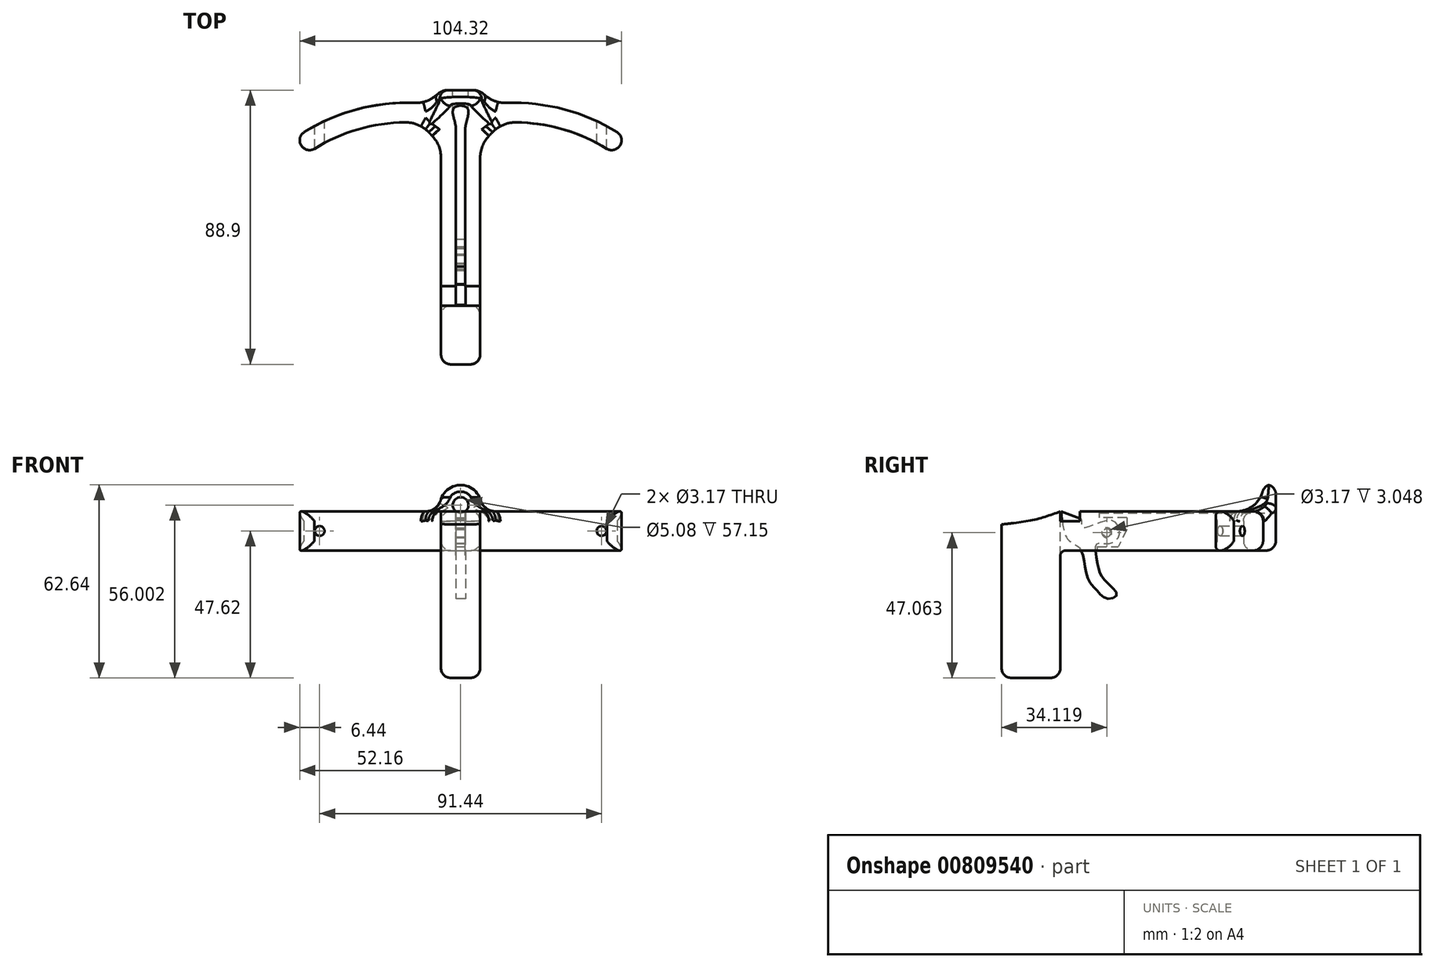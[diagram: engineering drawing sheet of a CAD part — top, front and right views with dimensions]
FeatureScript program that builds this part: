
annotation { "Feature Type Name" : "Feature", "Feature Type Description" : "" }
export const myFeature = defineFeature(function(context is Context, id is Id, definition is map)
    precondition{}
    {
        {
            var Q0;
            Q0=qCreatedBy(makeId("Top.planeOp"),FACE);
            var sketch = newSketch(context, id + "F0", { "sketchPlane" : qUnion([Q0])});
            skLineSegment(sketch, "E0.bottom", {"start": v(0, 0) * mm, "end": v(6.35, 0) * mm});
            skLineSegment(sketch, "E0.top", {"start": v(0, 76.2) * mm, "end": v(6.35, 76.2) * mm});
            skLineSegment(sketch, "E0.left", {"start": v(0, 0) * mm, "end": v(0, 76.2) * mm});
            skLineSegment(sketch, "E0.right", {"start": v(6.35, 0) * mm, "end": v(6.35, 58.42) * mm});
            skArc(sketch, "E1", {"start": v(50.8, 62.54) * mm, "mid": v(29.37, 70.92) * mm, "end": v(6.35, 71.12) * mm});
            skArc(sketch, "E2.0", {"start": v(47.45, 57.14) * mm, "mid": v(31.06, 64.05) * mm, "end": v(13.33, 65.59) * mm});
            skLineSegment(sketch, "E3", {"start": v(6.35, 58.42) * mm, "end": v(13.33, 65.59) * mm});
            skArc(sketch, "E4", {"start": v(47.45, 57.14) * mm, "mid": v(51.68, 58.26) * mm, "end": v(50.8, 62.54) * mm});
            skLineSegment(sketch, "E5.trimOffspring", {"start": v(6.35, 71.12) * mm, "end": v(6.35, 76.2) * mm});
            skLineSegment(sketch, "E6.MirrorCS", {"start": v(-6.35, 71.12) * mm, "end": v(-6.35, 76.2) * mm});
            skArc(sketch, "E7.MirrorCS", {"start": v(-47.45, 57.14) * mm, "mid": v(-51.68, 58.26) * mm, "end": v(-50.8, 62.54) * mm});
            skLineSegment(sketch, "E8.MirrorCS", {"start": v(-6.35, 58.42) * mm, "end": v(-13.34, 65.59) * mm});
            skArc(sketch, "E9.MirrorCS", {"start": v(-47.45, 57.14) * mm, "mid": v(-31.06, 64.05) * mm, "end": v(-13.34, 65.59) * mm});
            skArc(sketch, "E10.MirrorCS", {"start": v(-50.8, 62.54) * mm, "mid": v(-29.37, 70.92) * mm, "end": v(-6.35, 71.12) * mm});
            skLineSegment(sketch, "E11.MirrorCS", {"start": v(-6.35, 0) * mm, "end": v(-6.35, 58.42) * mm});
            skLineSegment(sketch, "E12", {"start": v(-6.35, 76.2) * mm, "end": v(0, 76.2) * mm});
            skLineSegment(sketch, "E13", {"start": v(-6.35, 0) * mm, "end": v(0, 0) * mm});
            skSolve(sketch);
        }
        {
            var Q0;
            Q0 = qSketchRegion(id + "F0", true);
            extrude(context, id + "F1", {"entities" : qUnion([Q0]), "depth" : 12.7 * mm, "offsetDistance" : 25.4 * mm});
        }
        {
            var Q0;
            Q0=makeQuery(id+"F1.opExtrude","SWEPT_EDGE",EDGE,{"disambiguationData":[OSD([sQuery(id+"F0.wireOp",EDGE,"E2.0"),sQuery(id+"F0.wireOp",EDGE,"E3")])]});
            var Q1;
            Q1=makeQuery(id+"F1.opExtrude","SWEPT_EDGE",EDGE,{"disambiguationData":[OSD([sQuery(id+"F0.wireOp",EDGE,"E0.right"),sQuery(id+"F0.wireOp",EDGE,"E3")])]});
            var Q2;
            Q2=makeQuery(id+"F1.opExtrude","SWEPT_EDGE",EDGE,{"disambiguationData":[OSD([sQuery(id+"F0.wireOp",EDGE,"E1"),sQuery(id+"F0.wireOp",EDGE,"E5.trimOffspring")])]});
            var Q3;
            Q3=makeQuery(id+"F1.opExtrude","SWEPT_EDGE",EDGE,{"disambiguationData":[OSD([sQuery(id+"F0.wireOp",EDGE,"E6.MirrorCS"),sQuery(id+"F0.wireOp",EDGE,"E10.MirrorCS")])]});
            var Q4;
            Q4=makeQuery(id+"F1.opExtrude","SWEPT_EDGE",EDGE,{"disambiguationData":[OSD([sQuery(id+"F0.wireOp",EDGE,"E8.MirrorCS"),sQuery(id+"F0.wireOp",EDGE,"E11.MirrorCS")])]});
            var Q5;
            Q5=makeQuery(id+"F1.opExtrude","SWEPT_EDGE",EDGE,{"disambiguationData":[OSD([sQuery(id+"F0.wireOp",EDGE,"E8.MirrorCS"),sQuery(id+"F0.wireOp",EDGE,"E9.MirrorCS")])]});
            fillet(context, id + "F2", {"entities" : qUnion([Q0, Q1, Q2, Q3, Q4, Q5]), "radius" : 10.16 * mm, "tangentPropagation" : true, "allowEdgeOverflow" : false});
        }
        {
            var Q0;
            Q0=makeQuery(id+"F1.opExtrude","SWEPT_FACE",FACE,{"disambiguationData":[OSD([sQuery(id+"F0.wireOp",EDGE,"E0.top"),sQuery(id+"F0.wireOp",EDGE,"E12")])]});
            var sketch = newSketch(context, id + "F3", { "sketchPlane" : qUnion([Q0])});
            skCircle(sketch, "E14", {"center": v(0, 14.73) * mm, "radius": 6.67 * mm});
            skCircle(sketch, "E15", {"center": v(0, 14.73) * mm, "radius": 2.54 * mm});
            skSolve(sketch);
        }
        {
            var Q0;
            Q0 = qSketchRegion(id + "F3", true);
            extrude(context, id + "F4", {"entities" : qUnion([Q0]), "operationType" : NewBodyOperationType.ADD, "oppositeDirection" : true, "depth" : 12.7 * mm, "offsetDistance" : 25.4 * mm});
        }
        {
            var Q0;
            Q0=qCreatedBy(makeId("Right.planeOp"),FACE);
            var sketch = newSketch(context, id + "F5", { "sketchPlane" : qUnion([Q0])});
            skCircle(sketch, "E16", {"center": v(63.5, 21.4) * mm, "radius": 8.7 * mm});
            skSolve(sketch);
        }
        {
            var Q0;
            Q0 = qSketchRegion(id + "F5", true);
            extrude(context, id + "F6", {"entities" : qUnion([Q0]), "operationType" : NewBodyOperationType.REMOVE, "endBound" : BoundingType.SYMMETRIC, "oppositeDirection" : true, "depth" : 25.4 * mm, "offsetDistance" : 25.4 * mm});
        }
        {
            var Q0;
            Q0=makeQuery(id+"F4.boolean.opBoolean","INTERSECT",EDGE,{"disambiguationData":[OD(0.0)],"derivedFrom":[makeQuery(id+"F1.opExtrude","CAP_FACE",FACE,{"disambiguationData":[OSD([sQuery(id+"F0.wireOp",EDGE,"E0.bottom"),sQuery(id+"F0.wireOp",EDGE,"E0.top"),sQuery(id+"F0.wireOp",EDGE,"E0.right"),sQuery(id+"F0.wireOp",EDGE,"E1"),sQuery(id+"F0.wireOp",EDGE,"E2.0"),sQuery(id+"F0.wireOp",EDGE,"E3"),sQuery(id+"F0.wireOp",EDGE,"E4"),sQuery(id+"F0.wireOp",EDGE,"E5.trimOffspring"),sQuery(id+"F0.wireOp",EDGE,"E6.MirrorCS"),sQuery(id+"F0.wireOp",EDGE,"E7.MirrorCS"),sQuery(id+"F0.wireOp",EDGE,"E8.MirrorCS"),sQuery(id+"F0.wireOp",EDGE,"E9.MirrorCS"),sQuery(id+"F0.wireOp",EDGE,"E10.MirrorCS"),sQuery(id+"F0.wireOp",EDGE,"E11.MirrorCS"),sQuery(id+"F0.wireOp",EDGE,"E12"),sQuery(id+"F0.wireOp",EDGE,"E13")])],"isStart":false}),makeQuery(id+"F4.opExtrude","SWEPT_FACE",FACE,{"disambiguationData":[OSD([sQuery(id+"F3.wireOp",EDGE,"E14")])]})]});
            var Q1;
            Q1=makeQuery(id+"F4.boolean.opBoolean","INTERSECT",EDGE,{"disambiguationData":[OD(1.0)],"derivedFrom":[makeQuery(id+"F1.opExtrude","CAP_FACE",FACE,{"disambiguationData":[OSD([sQuery(id+"F0.wireOp",EDGE,"E0.bottom"),sQuery(id+"F0.wireOp",EDGE,"E0.top"),sQuery(id+"F0.wireOp",EDGE,"E0.right"),sQuery(id+"F0.wireOp",EDGE,"E1"),sQuery(id+"F0.wireOp",EDGE,"E2.0"),sQuery(id+"F0.wireOp",EDGE,"E3"),sQuery(id+"F0.wireOp",EDGE,"E4"),sQuery(id+"F0.wireOp",EDGE,"E5.trimOffspring"),sQuery(id+"F0.wireOp",EDGE,"E6.MirrorCS"),sQuery(id+"F0.wireOp",EDGE,"E7.MirrorCS"),sQuery(id+"F0.wireOp",EDGE,"E8.MirrorCS"),sQuery(id+"F0.wireOp",EDGE,"E9.MirrorCS"),sQuery(id+"F0.wireOp",EDGE,"E10.MirrorCS"),sQuery(id+"F0.wireOp",EDGE,"E11.MirrorCS"),sQuery(id+"F0.wireOp",EDGE,"E12"),sQuery(id+"F0.wireOp",EDGE,"E13")])],"isStart":false}),makeQuery(id+"F4.opExtrude","SWEPT_FACE",FACE,{"disambiguationData":[OSD([sQuery(id+"F3.wireOp",EDGE,"E14")])]})]});
            fillet(context, id + "F7", {"entities" : qUnion([Q0, Q1]), "radius" : 5.08 * mm, "tangentPropagation" : true, "allowEdgeOverflow" : false});
        }
        {
            var Q0;
            Q0=makeQuery(id+"F4.boolean.opBoolean","MERGE",FACE,{"derivedFrom":[makeQuery(id+"F1.opExtrude","SWEPT_FACE",FACE,{"disambiguationData":[OSD([sQuery(id+"F0.wireOp",EDGE,"E0.top"),sQuery(id+"F0.wireOp",EDGE,"E12")])]}),makeQuery(id+"F4.opExtrude","CAP_FACE",FACE,{"disambiguationData":[OSD([sQuery(id+"F3.wireOp",EDGE,"E14"),sQuery(id+"F3.wireOp",EDGE,"E15")])],"isStart":true})]});
            var sketch = newSketch(context, id + "F8", { "sketchPlane" : qUnion([Q0])});
            skCircle(sketch, "E17", {"center": v(0, 14.73) * mm, "radius": 2.54 * mm});
            skSolve(sketch);
        }
        {
            var Q0;
            Q0 = qSketchRegion(id + "F8", true);
            extrude(context, id + "F9", {"entities" : qUnion([Q0]), "operationType" : NewBodyOperationType.REMOVE, "endBound" : BoundingType.THROUGH_ALL, "oppositeDirection" : true, "depth" : 25.4 * mm, "offsetDistance" : 25.4 * mm});
        }
        {
            var Q0;
            Q0=makeQuery(id+"F4.boolean.opBoolean","MERGE",FACE,{"derivedFrom":[makeQuery(id+"F1.opExtrude","SWEPT_FACE",FACE,{"disambiguationData":[OSD([sQuery(id+"F0.wireOp",EDGE,"E0.top"),sQuery(id+"F0.wireOp",EDGE,"E12")])]}),makeQuery(id+"F4.opExtrude","CAP_FACE",FACE,{"disambiguationData":[OSD([sQuery(id+"F3.wireOp",EDGE,"E14"),sQuery(id+"F3.wireOp",EDGE,"E15")])],"isStart":true})]});
            cPlane(context, id + "F10", {"entities" : qUnion([Q0]), "cplaneType" : CPlaneType.OFFSET, "offset" : 0 * mm, "width" : 152.4 * mm, "height" : 152.4 * mm});
        }
        {
            var Q0;
            Q0=makeQuery(id+"F1.opExtrude","SWEPT_FACE",FACE,{"disambiguationData":[OSD([sQuery(id+"F0.wireOp",EDGE,"E11.MirrorCS")])]});
            var sketch = newSketch(context, id + "F11", { "sketchPlane" : qUnion([Q0])});
            skLineSegment(sketch, "E18.bottom", {"start": v(0, 12.7) * mm, "end": v(-12.7, 12.7) * mm});
            skLineSegment(sketch, "E18.top", {"start": v(0, 9.52) * mm, "end": v(-12.7, 9.52) * mm});
            skLineSegment(sketch, "E18.left", {"start": v(0, 12.7) * mm, "end": v(0, 9.52) * mm});
            skLineSegment(sketch, "E18.right", {"start": v(-12.7, 12.7) * mm, "end": v(-12.7, 9.52) * mm});
            skSolve(sketch);
        }
        {
            var Q0;
            Q0 = qSketchRegion(id + "F11", true);
            extrude(context, id + "F12", {"entities" : qUnion([Q0]), "operationType" : NewBodyOperationType.REMOVE, "oppositeDirection" : true, "depth" : 25.4 * mm, "offsetDistance" : 25.4 * mm});
        }
        {
            var Q0;
            {var subQ0=sQuery(id+"F0.wireOp",EDGE,"E9.MirrorCS");var subQ1=sQuery(id+"F0.wireOp",EDGE,"E8.MirrorCS");var subQ2=sQuery(id+"F0.wireOp",EDGE,"E10.MirrorCS");var subQ3=sQuery(id+"F0.wireOp",EDGE,"E11.MirrorCS");var subQ4=sQuery(id+"F0.wireOp",EDGE,"E6.MirrorCS");var subQ5=sQuery(id+"F0.wireOp",EDGE,"E7.MirrorCS");var subQ6=sQuery(id+"F0.wireOp",EDGE,"E13");var subQ7=sQuery(id+"F0.wireOp",EDGE,"E0.bottom");var subQ9=sQuery(id+"F0.wireOp",EDGE,"E12");var subQ10=sQuery(id+"F0.wireOp",EDGE,"E5.trimOffspring");var subQ11=sQuery(id+"F0.wireOp",EDGE,"E4");var subQ12=sQuery(id+"F0.wireOp",EDGE,"E3");var subQ13=sQuery(id+"F0.wireOp",EDGE,"E2.0");var subQ14=sQuery(id+"F0.wireOp",EDGE,"E1");var subQ15=sQuery(id+"F0.wireOp",EDGE,"E0.right");var subQ16=sQuery(id+"F0.wireOp",EDGE,"E0.top");var subQ17=makeQuery(id+"F1.opExtrude","CAP_FACE",FACE,{"disambiguationData":[OSD([subQ7,subQ16,subQ15,subQ14,subQ13,subQ12,subQ11,subQ10,subQ4,subQ5,subQ1,subQ0,subQ2,subQ3,subQ9,subQ6])],"isStart":false});Q0=makeQuery(id+"F9.boolean.opBoolean","SPLIT",FACE,{"disambiguationData":[TD([makeQuery(id+"F1.opExtrude","SWEPT_FACE",FACE,{"disambiguationData":[OSD([subQ5])]})])],"derivedFrom":subQ17});}
            var sketch = newSketch(context, id + "F13", { "sketchPlane" : qUnion([Q0])});
            skLineSegment(sketch, "E19.bottom", {"start": v(-1.52, 19.05) * mm, "end": v(1.52, 19.05) * mm});
            skLineSegment(sketch, "E19.top", {"start": v(-1.52, 6.35) * mm, "end": v(1.52, 6.35) * mm});
            skLineSegment(sketch, "E19.left", {"start": v(-1.52, 19.05) * mm, "end": v(-1.52, 6.35) * mm});
            skLineSegment(sketch, "E19.right", {"start": v(1.52, 19.05) * mm, "end": v(1.52, 6.35) * mm});
            skSolve(sketch);
        }
        {
            var Q0;
            Q0 = qSketchRegion(id + "F13", true);
            extrude(context, id + "F14", {"entities" : qUnion([Q0]), "operationType" : NewBodyOperationType.REMOVE, "oppositeDirection" : true, "depth" : 25.4 * mm, "offsetDistance" : 25.4 * mm});
        }
        {
            var Q0;
            Q0=makeQuery(id+"F14.boolean.opBoolean","COPY",FACE,{"derivedFrom":makeQuery(id+"F14.opExtrude","SWEPT_FACE",FACE,{"disambiguationData":[OSD([sQuery(id+"F13.wireOp",EDGE,"E19.right")])]})});
            var Q1;
            Q1=makeQuery(id+"F14.boolean.opBoolean","COPY",FACE,{"derivedFrom":makeQuery(id+"F14.opExtrude","SWEPT_FACE",FACE,{"disambiguationData":[OSD([sQuery(id+"F13.wireOp",EDGE,"E19.left")])]})});
            cPlane(context, id + "F15", {"entities" : qUnion([Q0, Q1]), "cplaneType" : CPlaneType.MID_PLANE, "offset" : 25.4 * mm, "width" : 152.4 * mm, "height" : 152.4 * mm});
        }
        {
            var Q0;
            Q0=makeQuery(id+"F1.opExtrude","SWEPT_FACE",FACE,{"disambiguationData":[OSD([sQuery(id+"F0.wireOp",EDGE,"E0.bottom"),sQuery(id+"F0.wireOp",EDGE,"E13")])]});
            var sketch = newSketch(context, id + "F16", { "sketchPlane" : qUnion([Q0])});
            skPoint(sketch, "E20.oppositeSnap0", {"position": v(6.35, 4.76) * mm});
            skLineSegment(sketch, "E20.bottom", {"start": v(-6.35, 9.52) * mm, "end": v(6.35, 9.52) * mm});
            skLineSegment(sketch, "E20.top", {"start": v(-6.35, -41.28) * mm, "end": v(6.35, -41.28) * mm});
            skLineSegment(sketch, "E20.left", {"start": v(-6.35, 9.52) * mm, "end": v(-6.35, -41.28) * mm});
            skLineSegment(sketch, "E20.right", {"start": v(6.35, 9.52) * mm, "end": v(6.35, -41.28) * mm});
            skSolve(sketch);
        }
        {
            var Q0;
            Q0 = qSketchRegion(id + "F16", true);
            extrude(context, id + "F17", {"entities" : qUnion([Q0]), "operationType" : NewBodyOperationType.ADD, "endBound" : BoundingType.SYMMETRIC, "depth" : 12.7 * mm, "offsetDistance" : 25.4 * mm});
        }
        {
            var Q0;
            Q0=makeQuery(id+"F17.opExtrude","CAP_FACE",FACE,{"disambiguationData":[OSD([sQuery(id+"F16.wireOp",EDGE,"E20.bottom"),sQuery(id+"F16.wireOp",EDGE,"E20.top"),sQuery(id+"F16.wireOp",EDGE,"E20.left"),sQuery(id+"F16.wireOp",EDGE,"E20.right")])],"isStart":false});
            var sketch = newSketch(context, id + "F18", { "sketchPlane" : qUnion([Q0])});
            skLineSegment(sketch, "E21.bottom", {"start": v(-6.35, 9.52) * mm, "end": v(6.35, 9.52) * mm});
            skLineSegment(sketch, "E21.top", {"start": v(-6.35, -41.28) * mm, "end": v(6.35, -41.28) * mm});
            skLineSegment(sketch, "E21.left", {"start": v(-6.35, 9.52) * mm, "end": v(-6.35, -41.28) * mm});
            skLineSegment(sketch, "E21.right", {"start": v(6.35, 9.52) * mm, "end": v(6.35, -41.28) * mm});
            skSolve(sketch);
        }
        {
            var Q0;
            Q0 = qSketchRegion(id + "F18", true);
            extrude(context, id + "F19", {"entities" : qUnion([Q0]), "operationType" : NewBodyOperationType.ADD, "depth" : 6.35 * mm, "offsetDistance" : 25.4 * mm});
        }
        {
            var Q0;
            Q0=makeQuery(id+"F19.boolean.opBoolean","MERGE",FACE,{"derivedFrom":[makeQuery(id+"F17.boolean.opBoolean","MERGE",FACE,{"derivedFrom":[makeQuery(id+"F12.boolean.opBoolean","COPY",FACE,{"derivedFrom":makeQuery(id+"F12.opExtrude","SWEPT_FACE",FACE,{"disambiguationData":[OSD([sQuery(id+"F11.wireOp",EDGE,"E18.top")])]})}),makeQuery(id+"F17.opExtrude","SWEPT_FACE",FACE,{"disambiguationData":[OSD([sQuery(id+"F16.wireOp",EDGE,"E20.bottom")])]})]}),makeQuery(id+"F19.opExtrude","SWEPT_FACE",FACE,{"disambiguationData":[OSD([sQuery(id+"F18.wireOp",EDGE,"E21.bottom")])]})]});
            var sketch = newSketch(context, id + "F20", { "sketchPlane" : qUnion([Q0])});
            skLineSegment(sketch, "E22.bottom", {"start": v(-6.35, 6.35) * mm, "end": v(6.35, 6.35) * mm});
            skLineSegment(sketch, "E22.top", {"start": v(-6.35, -12.7) * mm, "end": v(6.35, -12.7) * mm});
            skLineSegment(sketch, "E22.left", {"start": v(-6.35, 6.35) * mm, "end": v(-6.35, -12.7) * mm});
            skLineSegment(sketch, "E22.right", {"start": v(6.35, 6.35) * mm, "end": v(6.35, -12.7) * mm});
            skSolve(sketch);
        }
        {
            var Q0;
            Q0 = qSketchRegion(id + "F20", true);
            extrude(context, id + "F21", {"entities" : qUnion([Q0]), "operationType" : NewBodyOperationType.ADD, "depth" : 3.17 * mm, "offsetDistance" : 25.4 * mm});
        }
        {
            var Q0;
            Q0=makeQuery(id+"F21.boolean.opBoolean","MERGE",FACE,{"derivedFrom":[makeQuery(id+"F19.boolean.opBoolean","MERGE",FACE,{"derivedFrom":[makeQuery(id+"F17.boolean.opBoolean","MERGE",FACE,{"derivedFrom":[makeQuery(id+"F1.opExtrude","SWEPT_FACE",FACE,{"disambiguationData":[OSD([sQuery(id+"F0.wireOp",EDGE,"E11.MirrorCS")])]}),makeQuery(id+"F17.opExtrude","SWEPT_FACE",FACE,{"disambiguationData":[OSD([sQuery(id+"F16.wireOp",EDGE,"E20.left")])]})]}),makeQuery(id+"F19.opExtrude","SWEPT_FACE",FACE,{"disambiguationData":[OSD([sQuery(id+"F18.wireOp",EDGE,"E21.left")])]})]}),makeQuery(id+"F21.opExtrude","SWEPT_FACE",FACE,{"disambiguationData":[OSD([sQuery(id+"F20.wireOp",EDGE,"E22.left")])]})]});
            var sketch = newSketch(context, id + "F22", { "sketchPlane" : qUnion([Q0])});
            skFitSpline(sketch, "E23", {"points": [v(-6.35, 12.7) * mm, v(1.52, 10.14) * mm, v(12.7, 8.48) * mm], "startDerivative": vector(16.21, -6.14) * mm, "endDerivative": vector(21.74, -2.4) * mm});
            skLineSegment(sketch, "E24", {"start": v(-6.35, 12.7) * mm, "end": v(12.7, 12.7) * mm});
            skLineSegment(sketch, "E25", {"start": v(12.7, 12.7) * mm, "end": v(12.7, 8.48) * mm});
            skSolve(sketch);
        }
        {
            var Q0;
            Q0 = qSketchRegion(id + "F22", true);
            extrude(context, id + "F23", {"entities" : qUnion([Q0]), "operationType" : NewBodyOperationType.REMOVE, "oppositeDirection" : true, "depth" : 25.4 * mm, "offsetDistance" : 25.4 * mm});
        }
        {
            var Q0;
            Q0=makeQuery(id+"F14.boolean.opBoolean","COPY",FACE,{"derivedFrom":makeQuery(id+"F14.opExtrude","SWEPT_FACE",FACE,{"disambiguationData":[OSD([sQuery(id+"F13.wireOp",EDGE,"E19.bottom")])]})});
            var sketch = newSketch(context, id + "F24", { "sketchPlane" : qUnion([Q0])});
            skLineSegment(sketch, "E26.bottom", {"start": v(-1.52, 10.67) * mm, "end": v(1.52, 10.67) * mm});
            skLineSegment(sketch, "E26.top", {"start": v(-1.52, -2.03) * mm, "end": v(1.52, -2.03) * mm});
            skLineSegment(sketch, "E26.left", {"start": v(-1.52, 10.67) * mm, "end": v(-1.52, -2.03) * mm});
            skLineSegment(sketch, "E26.right", {"start": v(1.52, 10.67) * mm, "end": v(1.52, -2.03) * mm});
            skSolve(sketch);
        }
        {
            var Q0;
            Q0 = qSketchRegion(id + "F24", true);
            extrude(context, id + "F25", {"entities" : qUnion([Q0]), "operationType" : NewBodyOperationType.REMOVE, "oppositeDirection" : true, "depth" : 8.9 * mm, "offsetDistance" : 25.4 * mm});
        }
        {
            var Q0;
            Q0=qCreatedBy(id+"F15.planeOp",FACE);
            var sketch = newSketch(context, id + "F26", { "sketchPlane" : qUnion([Q0])});
            skLineSegment(sketch, "E27", {"start": v(-13.17, 10.28) * mm, "end": v(-6.6, 12.66) * mm});
            skFitSpline(sketch, "E28", {"points": [v(-6.6, 12.66) * mm, v(-7.5, 6.64) * mm, v(-9.13, 3.26) * mm, v(-12.38, 1.03) * mm, v(-14.18, -3.58) * mm, v(-15.37, -9.36) * mm, v(-18.5, -13.27) * mm, v(-21.38, -15.56) * mm, v(-24.62, -14.47) * mm, v(-22.21, -11.02) * mm, v(-19.36, -7.7) * mm, v(-18.42, -4) * mm, v(-18.1, 2.1) * mm, v(-21.6, 2.22) * mm, v(-25.35, 4.8) * mm, v(-22.97, 9.73) * mm, v(-13.49, 7.53) * mm, v(-13.17, 10.28) * mm], "startDerivative": vector(-8.92, -104.87) * mm, "endDerivative": vector(31, 20.67) * mm});
            skCircle(sketch, "E29", {"center": v(-21.42, 5.8) * mm, "radius": 1.59 * mm});
            skSolve(sketch);
        }
        {
            var Q0;
            Q0 = qSketchRegion(id + "F26", true);
            extrude(context, id + "F27", {"entities" : qUnion([Q0]), "operationType" : NewBodyOperationType.ADD, "endBound" : BoundingType.SYMMETRIC, "depth" : 3.17 * mm, "offsetDistance" : 25.4 * mm});
        }
        {
            var Q0;
            Q0=qCreatedBy(id+"F15.planeOp",FACE);
            var sketch = newSketch(context, id + "F28", { "sketchPlane" : qUnion([Q0])});
            skCircle(sketch, "E30", {"center": v(-21.44, 5.77) * mm, "radius": 1.27 * mm});
            skSolve(sketch);
        }
        {
            var Q0;
            Q0 = qSketchRegion(id + "F28", true);
            extrude(context, id + "F29", {"entities" : qUnion([Q0]), "operationType" : NewBodyOperationType.ADD, "endBound" : BoundingType.SYMMETRIC, "depth" : 6.35 * mm, "offsetDistance" : 25.4 * mm});
        }
        {
            var Q0;
            Q0=makeQuery(id+"F25.boolean.opBoolean","MERGE",FACE,{"derivedFrom":[makeQuery(id+"F14.boolean.opBoolean","COPY",FACE,{"derivedFrom":makeQuery(id+"F14.opExtrude","SWEPT_FACE",FACE,{"disambiguationData":[OSD([sQuery(id+"F13.wireOp",EDGE,"E19.right")])]})}),makeQuery(id+"F25.opExtrude","SWEPT_FACE",FACE,{"disambiguationData":[OSD([sQuery(id+"F24.wireOp",EDGE,"E26.right")])]})]});
            var sketch = newSketch(context, id + "F30", { "sketchPlane" : qUnion([Q0])});
            skLineSegment(sketch, "E31.bottom", {"start": v(-27.94, 0) * mm, "end": v(-18.29, 0) * mm});
            skLineSegment(sketch, "E31.top", {"start": v(-27.94, 1.27) * mm, "end": v(-18.29, 1.27) * mm});
            skLineSegment(sketch, "E31.left", {"start": v(-27.94, 0) * mm, "end": v(-27.94, 1.27) * mm});
            skLineSegment(sketch, "E31.right", {"start": v(-18.29, 0) * mm, "end": v(-18.29, 1.27) * mm});
            skLineSegment(sketch, "E32", {"start": v(-25.11, 1.27) * mm, "end": v(-27.94, 6.83) * mm});
            skLineSegment(sketch, "E33", {"start": v(-27.94, 6.83) * mm, "end": v(-27.94, 1.27) * mm});
            skSolve(sketch);
        }
        {
            var Q0;
            Q0 = qSketchRegion(id + "F30", true);
            extrude(context, id + "F31", {"entities" : qUnion([Q0]), "operationType" : NewBodyOperationType.ADD, "depth" : 6.35 * mm, "offsetDistance" : 25.4 * mm});
        }
        {
            var Q0;
            {var subQ0=sQuery(id+"F0.wireOp",EDGE,"E11.MirrorCS");var subQ1=sQuery(id+"F11.wireOp",EDGE,"E18.right");Q0=makeQuery(id+"F12.boolean.opBoolean","COPY",EDGE,{"disambiguationData":[TD([makeQuery(id+"F1.opExtrude","SWEPT_FACE",FACE,{"disambiguationData":[OSD([subQ0])]})])],"derivedFrom":makeQuery(id+"F12.opExtrude","SWEPT_EDGE",EDGE,{"disambiguationData":[OSD([subQ0,sQuery(id+"F11.wireOp",EDGE,"E18.bottom"),subQ1])]})});}
            var Q1;
            {var subQ0=sQuery(id+"F0.wireOp",EDGE,"E11.MirrorCS");var subQ1=sQuery(id+"F0.wireOp",EDGE,"E0.right");var subQ2=sQuery(id+"F11.wireOp",EDGE,"E18.right");Q1=makeQuery(id+"F12.boolean.opBoolean","COPY",EDGE,{"disambiguationData":[TD([makeQuery(id+"F1.opExtrude","SWEPT_FACE",FACE,{"disambiguationData":[OSD([subQ1])]})])],"derivedFrom":makeQuery(id+"F12.opExtrude","SWEPT_EDGE",EDGE,{"disambiguationData":[OSD([subQ0,sQuery(id+"F11.wireOp",EDGE,"E18.bottom"),subQ2])]})});}
            var Q2;
            Q2=makeQuery(id+"F23.boolean.opBoolean","COPY",EDGE,{"derivedFrom":makeQuery(id+"F23.opExtrude","SWEPT_EDGE",EDGE,{"disambiguationData":[OSD([sQuery(id+"F18.wireOp",EDGE,"E21.left"),sQuery(id+"F20.wireOp",EDGE,"E22.top"),sQuery(id+"F20.wireOp",EDGE,"E22.left"),sQuery(id+"F22.wireOp",EDGE,"E23"),sQuery(id+"F22.wireOp",EDGE,"E25")])]})});
            var Q3;
            Q3=makeQuery(id+"F17.boolean.opBoolean","INTERSECT",EDGE,{"disambiguationData":[OD(0.0)],"derivedFrom":[makeQuery(id+"F1.opExtrude","CAP_FACE",FACE,{"disambiguationData":[OSD([sQuery(id+"F0.wireOp",EDGE,"E0.bottom"),sQuery(id+"F0.wireOp",EDGE,"E0.top"),sQuery(id+"F0.wireOp",EDGE,"E0.right"),sQuery(id+"F0.wireOp",EDGE,"E1"),sQuery(id+"F0.wireOp",EDGE,"E2.0"),sQuery(id+"F0.wireOp",EDGE,"E3"),sQuery(id+"F0.wireOp",EDGE,"E4"),sQuery(id+"F0.wireOp",EDGE,"E5.trimOffspring"),sQuery(id+"F0.wireOp",EDGE,"E6.MirrorCS"),sQuery(id+"F0.wireOp",EDGE,"E7.MirrorCS"),sQuery(id+"F0.wireOp",EDGE,"E8.MirrorCS"),sQuery(id+"F0.wireOp",EDGE,"E9.MirrorCS"),sQuery(id+"F0.wireOp",EDGE,"E10.MirrorCS"),sQuery(id+"F0.wireOp",EDGE,"E11.MirrorCS"),sQuery(id+"F0.wireOp",EDGE,"E12"),sQuery(id+"F0.wireOp",EDGE,"E13")])],"isStart":true}),makeQuery(id+"F17.opExtrude","CAP_FACE",FACE,{"disambiguationData":[OSD([sQuery(id+"F16.wireOp",EDGE,"E20.bottom"),sQuery(id+"F16.wireOp",EDGE,"E20.top"),sQuery(id+"F16.wireOp",EDGE,"E20.left"),sQuery(id+"F16.wireOp",EDGE,"E20.right")])],"isStart":true})]});
            var Q4;
            Q4=makeQuery(id+"F17.boolean.opBoolean","INTERSECT",EDGE,{"disambiguationData":[OD(1.0)],"derivedFrom":[makeQuery(id+"F1.opExtrude","CAP_FACE",FACE,{"disambiguationData":[OSD([sQuery(id+"F0.wireOp",EDGE,"E0.bottom"),sQuery(id+"F0.wireOp",EDGE,"E0.top"),sQuery(id+"F0.wireOp",EDGE,"E0.right"),sQuery(id+"F0.wireOp",EDGE,"E1"),sQuery(id+"F0.wireOp",EDGE,"E2.0"),sQuery(id+"F0.wireOp",EDGE,"E3"),sQuery(id+"F0.wireOp",EDGE,"E4"),sQuery(id+"F0.wireOp",EDGE,"E5.trimOffspring"),sQuery(id+"F0.wireOp",EDGE,"E6.MirrorCS"),sQuery(id+"F0.wireOp",EDGE,"E7.MirrorCS"),sQuery(id+"F0.wireOp",EDGE,"E8.MirrorCS"),sQuery(id+"F0.wireOp",EDGE,"E9.MirrorCS"),sQuery(id+"F0.wireOp",EDGE,"E10.MirrorCS"),sQuery(id+"F0.wireOp",EDGE,"E11.MirrorCS"),sQuery(id+"F0.wireOp",EDGE,"E12"),sQuery(id+"F0.wireOp",EDGE,"E13")])],"isStart":true}),makeQuery(id+"F17.opExtrude","CAP_FACE",FACE,{"disambiguationData":[OSD([sQuery(id+"F16.wireOp",EDGE,"E20.bottom"),sQuery(id+"F16.wireOp",EDGE,"E20.top"),sQuery(id+"F16.wireOp",EDGE,"E20.left"),sQuery(id+"F16.wireOp",EDGE,"E20.right")])],"isStart":true})]});
            fillet(context, id + "F32", {"entities" : qUnion([Q0, Q1, Q2, Q3, Q4]), "radius" : 1.59 * mm, "tangentPropagation" : true, "allowEdgeOverflow" : false});
        }
        {
            var Q0;
            Q0=makeQuery(id+"F21.boolean.opBoolean","MERGE",EDGE,{"derivedFrom":[makeQuery(id+"F19.opExtrude","CAP_EDGE",EDGE,{"disambiguationData":[OSD([sQuery(id+"F18.wireOp",EDGE,"E21.left")])],"isStart":false}),makeQuery(id+"F21.opExtrude","SWEPT_EDGE",EDGE,{"disambiguationData":[OSD([sQuery(id+"F20.wireOp",EDGE,"E22.top"),sQuery(id+"F20.wireOp",EDGE,"E22.left")])]})]});
            var Q1;
            Q1=makeQuery(id+"F21.boolean.opBoolean","MERGE",EDGE,{"derivedFrom":[makeQuery(id+"F19.opExtrude","CAP_EDGE",EDGE,{"disambiguationData":[OSD([sQuery(id+"F18.wireOp",EDGE,"E21.right")])],"isStart":false}),makeQuery(id+"F21.opExtrude","SWEPT_EDGE",EDGE,{"disambiguationData":[OSD([sQuery(id+"F20.wireOp",EDGE,"E22.top"),sQuery(id+"F20.wireOp",EDGE,"E22.right")])]})]});
            var Q2;
            Q2=makeQuery(id+"F17.opExtrude","CAP_EDGE",EDGE,{"disambiguationData":[OSD([sQuery(id+"F16.wireOp",EDGE,"E20.left")])],"isStart":true});
            var Q3;
            Q3=makeQuery(id+"F17.opExtrude","CAP_EDGE",EDGE,{"disambiguationData":[OSD([sQuery(id+"F16.wireOp",EDGE,"E20.right")])],"isStart":true});
            var Q4;
            Q4=makeQuery(id+"F19.boolean.opBoolean","MERGE",EDGE,{"derivedFrom":[makeQuery(id+"F17.opExtrude","SWEPT_EDGE",EDGE,{"disambiguationData":[OSD([sQuery(id+"F16.wireOp",EDGE,"E20.top"),sQuery(id+"F16.wireOp",EDGE,"E20.right")])]}),makeQuery(id+"F19.opExtrude","SWEPT_EDGE",EDGE,{"disambiguationData":[OSD([sQuery(id+"F18.wireOp",EDGE,"E21.top"),sQuery(id+"F18.wireOp",EDGE,"E21.right")])]})]});
            var Q5;
            Q5=makeQuery(id+"F17.opExtrude","CAP_EDGE",EDGE,{"disambiguationData":[OSD([sQuery(id+"F16.wireOp",EDGE,"E20.top")])],"isStart":true});
            var Q6;
            Q6=makeQuery(id+"F19.opExtrude","CAP_EDGE",EDGE,{"disambiguationData":[OSD([sQuery(id+"F18.wireOp",EDGE,"E21.top")])],"isStart":false});
            var Q7;
            Q7=makeQuery(id+"F19.boolean.opBoolean","MERGE",EDGE,{"derivedFrom":[makeQuery(id+"F17.opExtrude","SWEPT_EDGE",EDGE,{"disambiguationData":[OSD([sQuery(id+"F16.wireOp",EDGE,"E20.top"),sQuery(id+"F16.wireOp",EDGE,"E20.left")])]}),makeQuery(id+"F19.opExtrude","SWEPT_EDGE",EDGE,{"disambiguationData":[OSD([sQuery(id+"F18.wireOp",EDGE,"E21.top"),sQuery(id+"F18.wireOp",EDGE,"E21.left")])]})]});
            var Q8;
            Q8=makeQuery(id+"F1.opExtrude","CAP_EDGE",EDGE,{"disambiguationData":[OSD([sQuery(id+"F0.wireOp",EDGE,"E1")])],"isStart":true});
            var Q9;
            Q9=makeQuery(id+"F1.opExtrude","CAP_EDGE",EDGE,{"disambiguationData":[OSD([sQuery(id+"F0.wireOp",EDGE,"E0.top"),sQuery(id+"F0.wireOp",EDGE,"E12")])],"isStart":true});
            var Q10;
            Q10=makeQuery(id+"F1.opExtrude","CAP_EDGE",EDGE,{"disambiguationData":[OSD([sQuery(id+"F0.wireOp",EDGE,"E10.MirrorCS")])],"isStart":true});
            var Q11;
            Q11=makeQuery(id+"F1.opExtrude","CAP_EDGE",EDGE,{"disambiguationData":[OSD([sQuery(id+"F0.wireOp",EDGE,"E9.MirrorCS")])],"isStart":false});
            var Q12;
            Q12=makeQuery(id+"F1.opExtrude","CAP_EDGE",EDGE,{"disambiguationData":[OSD([sQuery(id+"F0.wireOp",EDGE,"E10.MirrorCS")])],"isStart":false});
            var Q13;
            Q13=makeQuery(id+"F1.opExtrude","CAP_EDGE",EDGE,{"disambiguationData":[OSD([sQuery(id+"F0.wireOp",EDGE,"E2.0")])],"isStart":false});
            var Q14;
            Q14=makeQuery(id+"F1.opExtrude","CAP_EDGE",EDGE,{"disambiguationData":[OSD([sQuery(id+"F0.wireOp",EDGE,"E1")])],"isStart":false});
            var Q15;
            Q15=makeQuery(id+"F4.opExtrude","CAP_EDGE",EDGE,{"disambiguationData":[OSD([sQuery(id+"F3.wireOp",EDGE,"E14")])],"isStart":true});
            var Q16;
            Q16=makeQuery(id+"F6.boolean.opBoolean","INTERSECT",EDGE,{"derivedFrom":[makeQuery(id+"F4.opExtrude","SWEPT_FACE",FACE,{"disambiguationData":[OSD([sQuery(id+"F3.wireOp",EDGE,"E14")])]}),makeQuery(id+"F6.opExtrude","SWEPT_FACE",FACE,{"disambiguationData":[OSD([sQuery(id+"F5.wireOp",EDGE,"E16")])]})]});
            fillet(context, id + "F33", {"entities" : qUnion([Q0, Q1, Q2, Q3, Q4, Q5, Q6, Q7, Q8, Q9, Q10, Q11, Q12, Q13, Q14, Q15, Q16]), "radius" : 3.17 * mm, "tangentPropagation" : true, "allowEdgeOverflow" : false});
        }
        {
            var Q0;
            Q0=qCreatedBy(id+"F10.planeOp",FACE);
            var sketch = newSketch(context, id + "F34", { "sketchPlane" : qUnion([Q0])});
            skCircle(sketch, "E34", {"center": v(-45.72, 6.35) * mm, "radius": 1.59 * mm});
            skCircle(sketch, "E35", {"center": v(45.72, 6.35) * mm, "radius": 1.59 * mm});
            skLineSegment(sketch, "E36", {"start": v(0, 6.35) * mm, "end": v(45.72, 6.35) * mm, "construction": true});
            skLineSegment(sketch, "E37", {"start": v(0, 6.35) * mm, "end": v(-45.72, 6.35) * mm, "construction": true});
            skSolve(sketch);
        }
        {
            var Q0;
            Q0 = qSketchRegion(id + "F34", true);
            extrude(context, id + "F35", {"entities" : qUnion([Q0]), "operationType" : NewBodyOperationType.REMOVE, "oppositeDirection" : true, "depth" : 25.4 * mm, "offsetDistance" : 25.4 * mm});
        }
        {
            var Q0;
            Q0=makeQuery(id+"F2.opFillet","BLEND_EDGE",EDGE,{"blendedFrom":[makeQuery(id+"F1.opExtrude","SWEPT_EDGE",EDGE,{"disambiguationData":[OSD([sQuery(id+"F0.wireOp",EDGE,"E6.MirrorCS"),sQuery(id+"F0.wireOp",EDGE,"E10.MirrorCS")])]}),makeQuery(id+"F1.opExtrude","SWEPT_FACE",FACE,{"disambiguationData":[OSD([sQuery(id+"F0.wireOp",EDGE,"E0.top"),sQuery(id+"F0.wireOp",EDGE,"E12")])]})],"blendedInto":[makeQuery(id+"F1.opExtrude","SWEPT_FACE",FACE,{"disambiguationData":[OSD([sQuery(id+"F0.wireOp",EDGE,"E0.top"),sQuery(id+"F0.wireOp",EDGE,"E12")])]})]});
            var Q1;
            Q1=makeQuery(id+"F2.opFillet","BLEND_EDGE",EDGE,{"blendedFrom":[makeQuery(id+"F1.opExtrude","SWEPT_EDGE",EDGE,{"disambiguationData":[OSD([sQuery(id+"F0.wireOp",EDGE,"E1"),sQuery(id+"F0.wireOp",EDGE,"E5.trimOffspring")])]}),makeQuery(id+"F1.opExtrude","SWEPT_FACE",FACE,{"disambiguationData":[OSD([sQuery(id+"F0.wireOp",EDGE,"E0.top"),sQuery(id+"F0.wireOp",EDGE,"E12")])]})],"blendedInto":[makeQuery(id+"F1.opExtrude","SWEPT_FACE",FACE,{"disambiguationData":[OSD([sQuery(id+"F0.wireOp",EDGE,"E0.top"),sQuery(id+"F0.wireOp",EDGE,"E12")])]})]});
            fillet(context, id + "F36", {"entities" : qUnion([Q0, Q1]), "radius" : 5.08 * mm, "tangentPropagation" : true, "allowEdgeOverflow" : false});
        }
    });
